# Revit family: Haworth_Masters_Table_Square
name_source: partatom
category: Furniture Systems
revit_build: Autodesk Revit 2018 (Build: 20170223_1515(x64)
units: mm (PartAtom-declared; Revit-internal decimal feet)

## family parameters
Always vertical = Yes
Cut with Voids When Loaded = No
OmniClass Number = 23.40.70.14.64.21
OmniClass Title = Systems Furniture
Part Type = Normal
Room Calculation Point = No
Round Connector Dimension = Use Diameter
Shared = No
Work Plane-Based = No

## types (4) — shared parameters
Actual Height = 29 1/4"
Assembly Code = E2020200
Custom Size = No
Leg Height = 28 1/16"
Manufacturer = Haworth
Max. Width = 48"
Min. Width = 30"
Min/Max Height = 29 1/4 in.
Min/Max Width = 30, 36, 42, 48 in.
Model = Masters Series
Revision Number = 1
Size = Verify Final Dim. w/ Haworth
Sustainability Info = http://media.haworth.com
Table Thickness = 1 3/16"
URL = http://www.haworth.com
URL - Product = http://www.haworth.com
Warranty = http://www.haworth.com

## per-type parameters (varying)
| type | Actual Width | Description | Disc Base Radius | Width |
| 30d 30w | 30" | Masters Square Table - 30w | 10 1/2" | 30" |
| 36d 36w | 36" | Masters Square Table - 36w | 13 1/2" | 36" |
| 42d 42w | 42" | Masters Square Table - 42w | 13 1/2" | 42" |
| 48d 48w | 48" | Masters Square Table - 48w | 13 1/2" | 48" |

## geometry (parser evidence)
native form markers: Sweep x6
no freeform markers — native parametric forms only
